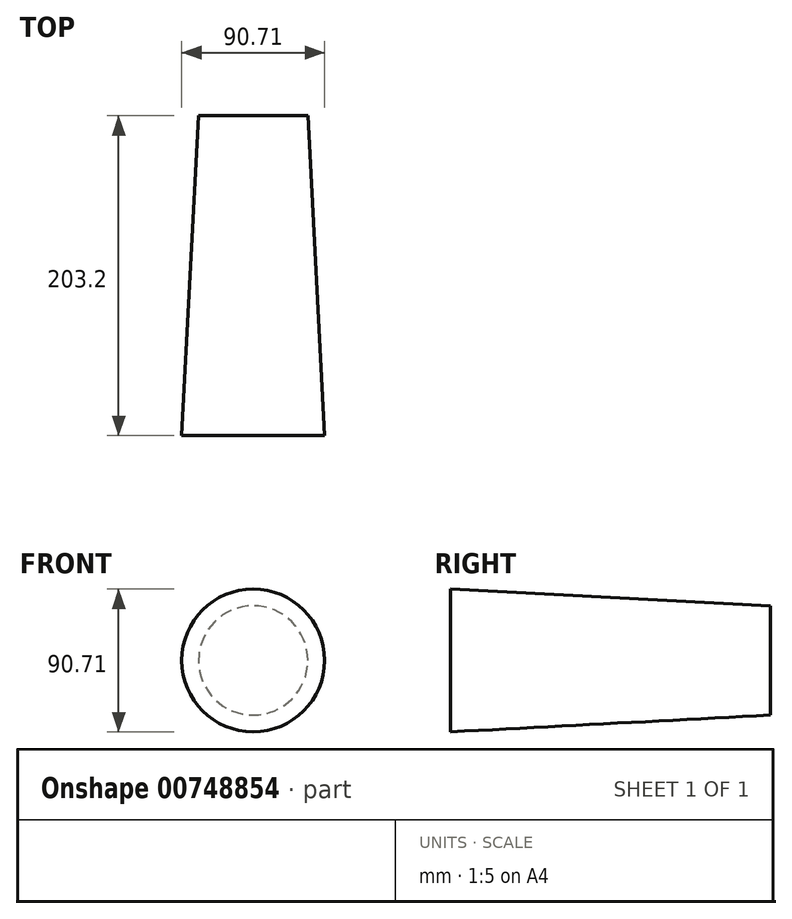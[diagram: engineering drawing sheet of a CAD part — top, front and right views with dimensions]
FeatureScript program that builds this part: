
annotation { "Feature Type Name" : "Feature", "Feature Type Description" : "" }
export const myFeature = defineFeature(function(context is Context, id is Id, definition is map)
    precondition{}
    {
        {
            var Q0;
            Q0=qCreatedBy(makeId("Front.planeOp"),FACE);
            var sketch = newSketch(context, id + "F0", { "sketchPlane" : qUnion([Q0])});
            skCircle(sketch, "E0", {"center": v(-14, 45.78) * mm, "radius": 34.7 * mm});
            skSolve(sketch);
        }
        {
            var Q0;
            Q0 = qSketchRegion(id + "F0", true);
            extrude(context, id + "F1", {"entities" : qUnion([Q0]), "depth" : 203.2 * mm, "offsetDistance" : 25.4 * mm, "hasDraft" : true, "draftAngle" : 3 * degree});
        }
    });
